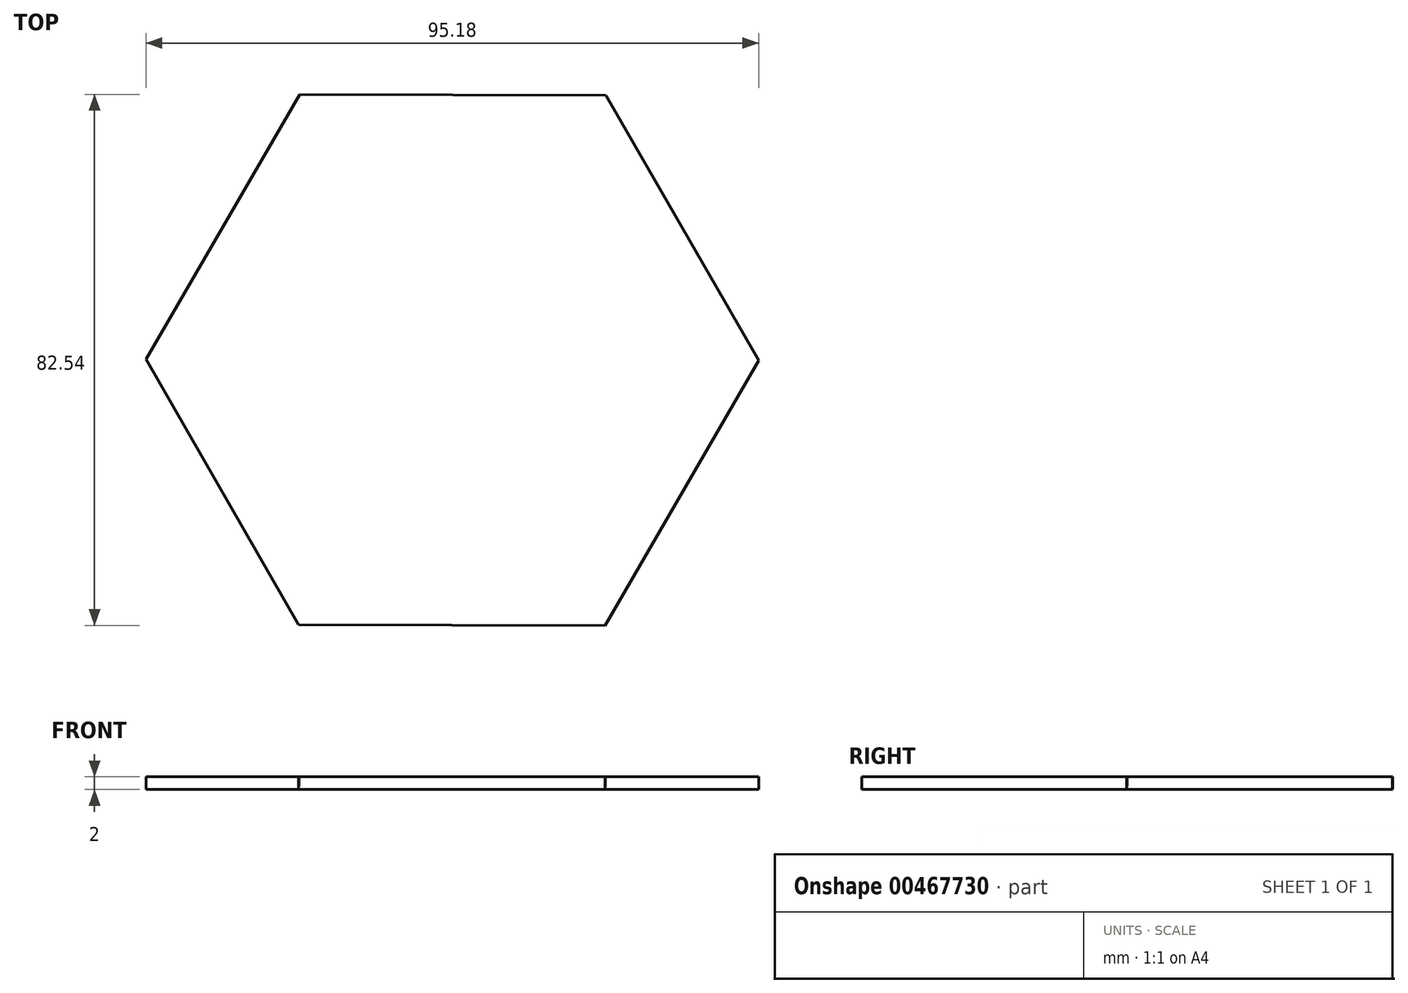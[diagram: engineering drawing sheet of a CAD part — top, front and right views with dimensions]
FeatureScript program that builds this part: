
annotation { "Feature Type Name" : "Feature", "Feature Type Description" : "" }
export const myFeature = defineFeature(function(context is Context, id is Id, definition is map)
    precondition{}
    {
        {
            var Q0;
            Q0=qCreatedBy(makeId("Top.planeOp"),FACE);
            var sketch = newSketch(context, id + "F0", { "sketchPlane" : qUnion([Q0])});
            skCircle(sketch, "E0.cCircle", {"center": v(0, 0) * mm, "radius": 41.22 * mm, "construction": true});
            skLineSegment(sketch, "E0.0", {"start": v(47.6, -0.1) * mm, "end": v(23.7, -41.27) * mm});
            skLineSegment(sketch, "E0.1", {"start": v(23.7, -41.27) * mm, "end": v(-23.88, -41.17) * mm});
            skLineSegment(sketch, "E0.2", {"start": v(-23.88, -41.17) * mm, "end": v(-47.6, 0.1) * mm});
            skLineSegment(sketch, "E0.3", {"start": v(-47.6, 0.1) * mm, "end": v(-23.7, 41.27) * mm});
            skLineSegment(sketch, "E0.4", {"start": v(-23.7, 41.27) * mm, "end": v(23.88, 41.17) * mm});
            skLineSegment(sketch, "E0.5", {"start": v(23.88, 41.17) * mm, "end": v(47.6, -0.1) * mm});
            skPoint(sketch, "E0.0.midPoint", {"position": v(35.65, -20.68) * mm});
            skSolve(sketch);
        }
        {
            var Q0;
            Q0=makeQuery(id+"F0.imprint","IMPRINT",FACE,{"disambiguationData":[TD([[makeQuery(id+"F0.imprint","IMPRINT",EDGE,{"derivedFrom":sQuery(id+"F0.wireOp",EDGE,"E0.0")}),-1.0]])]});
            extrude(context, id + "F1", {"entities" : qUnion([Q0]), "depth" : 2 * mm});
        }
    });
